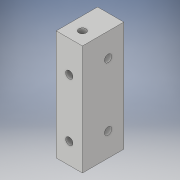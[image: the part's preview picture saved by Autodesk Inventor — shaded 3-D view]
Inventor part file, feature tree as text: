
AUTODESK INVENTOR PART (.ipt)
format: ipt  version: 2019 (Build 230136000, 136)  size: 130,048 bytes
history: native  units: mm
features: sketch x5, hole x4, other x1, extrude x1
ambient origin geometry x8: Origin, YZ Plane, XZ Plane, XY Plane, X Axis, Y Axis, Z Axis, Center Point
bodies: Body1 (feature_tree)
feature tree (11):
  other  "Твердое тело1"
  extrude  "Выдавливание1"  Depth=10.0mm
  hole  "Отверстие1"  [1 undecoded]
  hole  "Отверстие2"  [1 undecoded]
  hole  "Отверстие5"  [1 undecoded]
  hole  "Отверстие6"  [1 undecoded]
  sketch  "Эскиз1"
  sketch  "Эскиз2"
  sketch  "Эскиз3"
  sketch  "Эскиз7"
  sketch  "Эскиз9"
note: 4 required parameter values undecoded (feature->parameter linkage not recoverable at this tier; creation-order binding heuristic only, values carry confidence <= 0.55)
